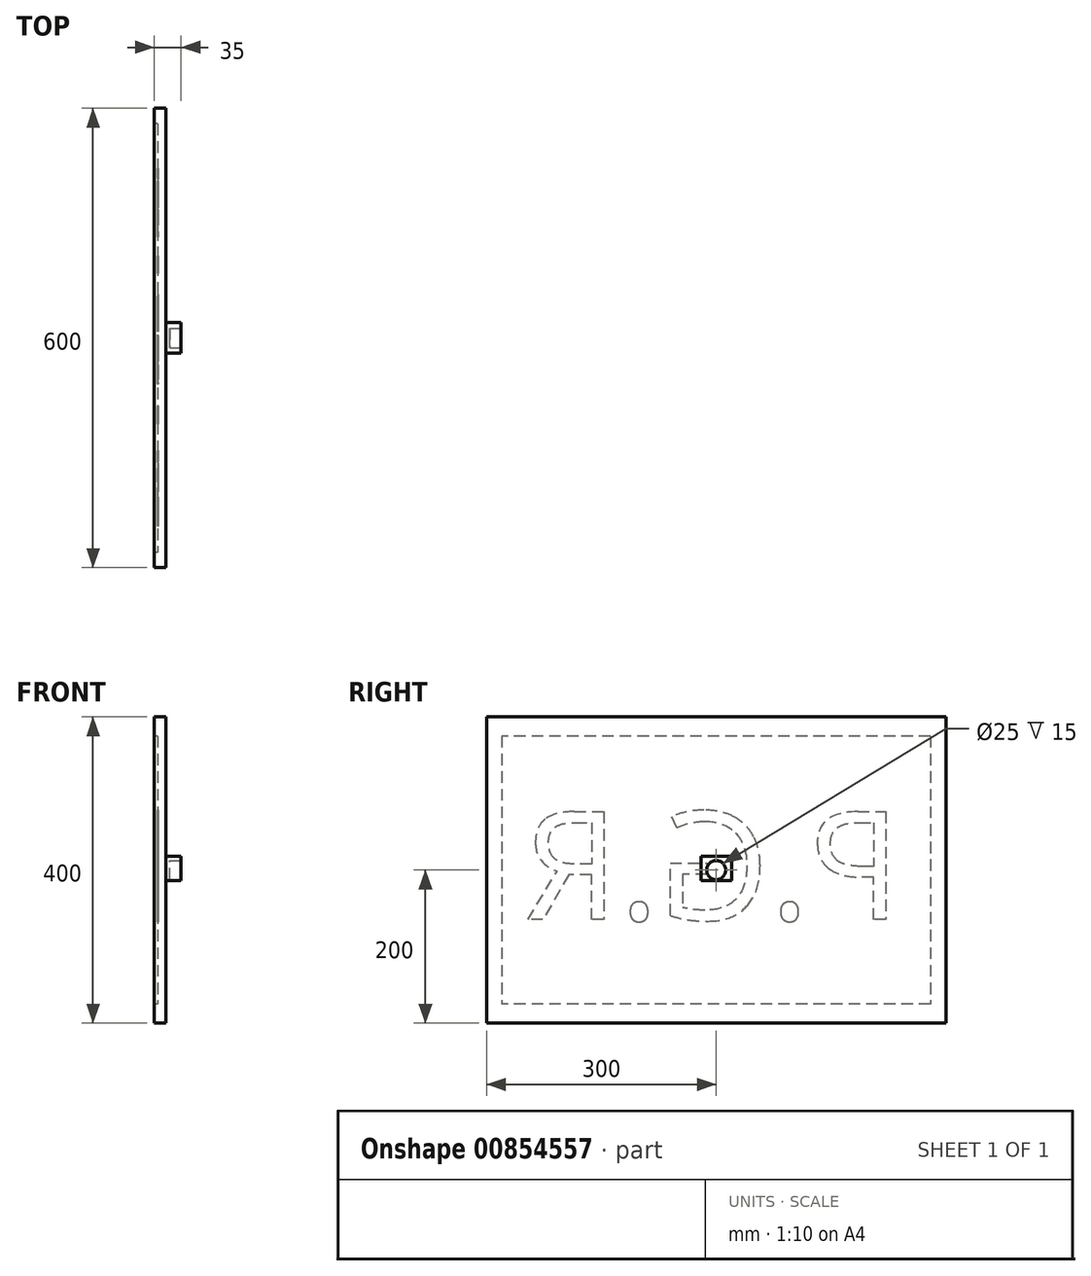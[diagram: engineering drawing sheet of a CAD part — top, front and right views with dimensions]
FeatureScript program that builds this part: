
annotation { "Feature Type Name" : "Feature", "Feature Type Description" : "" }
export const myFeature = defineFeature(function(context is Context, id is Id, definition is map)
    precondition{}
    {
        {
            var Q0;
            Q0=qCreatedBy(makeId("Right.planeOp"),FACE);
            var sketch = newSketch(context, id + "F0", { "sketchPlane" : qUnion([Q0])});
            skLineSegment(sketch, "E0.bottom", {"start": v(-300, 200) * mm, "end": v(300, 200) * mm});
            skLineSegment(sketch, "E0.top", {"start": v(-300, -200) * mm, "end": v(300, -200) * mm});
            skLineSegment(sketch, "E0.left", {"start": v(-300, 200) * mm, "end": v(-300, -200) * mm});
            skLineSegment(sketch, "E0.right", {"start": v(300, 200) * mm, "end": v(300, -200) * mm});
            skSolve(sketch);
        }
        {
            var Q0;
            Q0=makeQuery(id+"F0.imprint","IMPRINT",FACE,{"disambiguationData":[TD([[makeQuery(id+"F0.imprint","IMPRINT",EDGE,{"derivedFrom":sQuery(id+"F0.wireOp",EDGE,"E0.bottom")}),-1.0]])]});
            var sketch = newSketch(context, id + "F1", { "sketchPlane" : qUnion([Q0])});
            skLineSegment(sketch, "E1.bottom", {"start": v(-20, 18) * mm, "end": v(20, 18) * mm});
            skLineSegment(sketch, "E1.top", {"start": v(-20, -14) * mm, "end": v(20, -14) * mm});
            skLineSegment(sketch, "E1.left", {"start": v(-20, 18) * mm, "end": v(-20, -14) * mm});
            skLineSegment(sketch, "E1.right", {"start": v(20, 18) * mm, "end": v(20, -14) * mm});
            skSolve(sketch);
        }
        {
            var Q0;
            Q0=qSketchRegion(id+"F1",true);
            extrude(context, id + "F2", {"entities" : qUnion([Q0]), "depth" : 20 * mm, "offsetDistance" : 25 * mm});
        }
        {
            var Q0;
            Q0=makeQuery(id+"F0.imprint","IMPRINT",FACE,{"disambiguationData":[TD([[makeQuery(id+"F0.imprint","IMPRINT",EDGE,{"derivedFrom":sQuery(id+"F0.wireOp",EDGE,"E0.bottom")}),-1.0]])]});
            extrude(context, id + "F3", {"entities" : qUnion([Q0]), "operationType" : NewBodyOperationType.ADD, "oppositeDirection" : true, "depth" : 15 * mm, "offsetDistance" : 25 * mm});
        }
        {
            var Q0;
            Q0=makeQuery(id+"F2.opExtrude","CAP_FACE",FACE,{"disambiguationData":[OSD([sQuery(id+"F1.wireOp",EDGE,"E1.bottom"),sQuery(id+"F1.wireOp",EDGE,"E1.top"),sQuery(id+"F1.wireOp",EDGE,"E1.left"),sQuery(id+"F1.wireOp",EDGE,"E1.right")])],"isStart":false});
            var sketch = newSketch(context, id + "F4", { "sketchPlane" : qUnion([Q0])});
            skCircle(sketch, "E2", {"center": v(0, 0) * mm, "radius": 12.5 * mm});
            skSolve(sketch);
        }
        {
            var Q0;
            Q0=qSketchRegion(id+"F4",true);
            extrude(context, id + "F5", {"entities" : qUnion([Q0]), "operationType" : NewBodyOperationType.REMOVE, "oppositeDirection" : true, "depth" : 15 * mm, "offsetDistance" : 25 * mm});
        }
        {
            var Q0;
            Q0=makeQuery(id+"F3.opExtrude","CAP_FACE",FACE,{"disambiguationData":[OSD([sQuery(id+"F0.wireOp",EDGE,"E0.bottom"),sQuery(id+"F0.wireOp",EDGE,"E0.top"),sQuery(id+"F0.wireOp",EDGE,"E0.left"),sQuery(id+"F0.wireOp",EDGE,"E0.right")])],"isStart":false});
            var sketch = newSketch(context, id + "F6", { "sketchPlane" : qUnion([Q0])});
            skText(sketch, "E3", { "text": "P.G.R", "fontName": "OpenSans-Regular.ttf"});
            const initialGuessF6  = {"E3": [-0.24114, -0.0648, 1, 0, 0.1424]};
            skSetInitialGuess(sketch, initialGuessF6);
            skSolve(sketch);
        }
        {
            var Q0;
            Q0=qSketchRegion(id+"F6",true);
            extrude(context, id + "F7", {"entities" : qUnion([Q0]), "operationType" : NewBodyOperationType.REMOVE, "oppositeDirection" : true, "depth" : 5 * mm, "offsetDistance" : 25 * mm});
        }
        {
            var Q0;
            {var subQ0=sQuery(id+"F0.wireOp",EDGE,"E0.bottom");var subQ1=sQuery(id+"F0.wireOp",EDGE,"E0.right");var subQ2=sQuery(id+"F0.wireOp",EDGE,"E0.top");var subQ3=sQuery(id+"F0.wireOp",EDGE,"E0.left");Q0=makeQuery(id+"F7.boolean.opBoolean","SPLIT",FACE,{"disambiguationData":[TD([makeQuery(id+"F3.opExtrude","SWEPT_FACE",FACE,{"disambiguationData":[OSD([subQ0])]})])],"derivedFrom":makeQuery(id+"F3.opExtrude","CAP_FACE",FACE,{"disambiguationData":[OSD([subQ0,subQ2,subQ3,subQ1])],"isStart":false})});}
            var sketch = newSketch(context, id + "F8", { "sketchPlane" : qUnion([Q0])});
            skLineSegment(sketch, "E4.bottom", {"start": v(-280, 175) * mm, "end": v(280, 175) * mm});
            skLineSegment(sketch, "E4.top", {"start": v(-280, -175) * mm, "end": v(280, -175) * mm});
            skLineSegment(sketch, "E4.left", {"start": v(-280, 175) * mm, "end": v(-280, -175) * mm});
            skLineSegment(sketch, "E4.right", {"start": v(280, 175) * mm, "end": v(280, -175) * mm});
            skSolve(sketch);
        }
        {
            var Q0;
            Q0=qSketchRegion(id+"F8",true);
            extrude(context, id + "F9", {"entities" : qUnion([Q0]), "operationType" : NewBodyOperationType.REMOVE, "oppositeDirection" : true, "depth" : 4 * mm, "offsetDistance" : 25 * mm});
        }
    });
